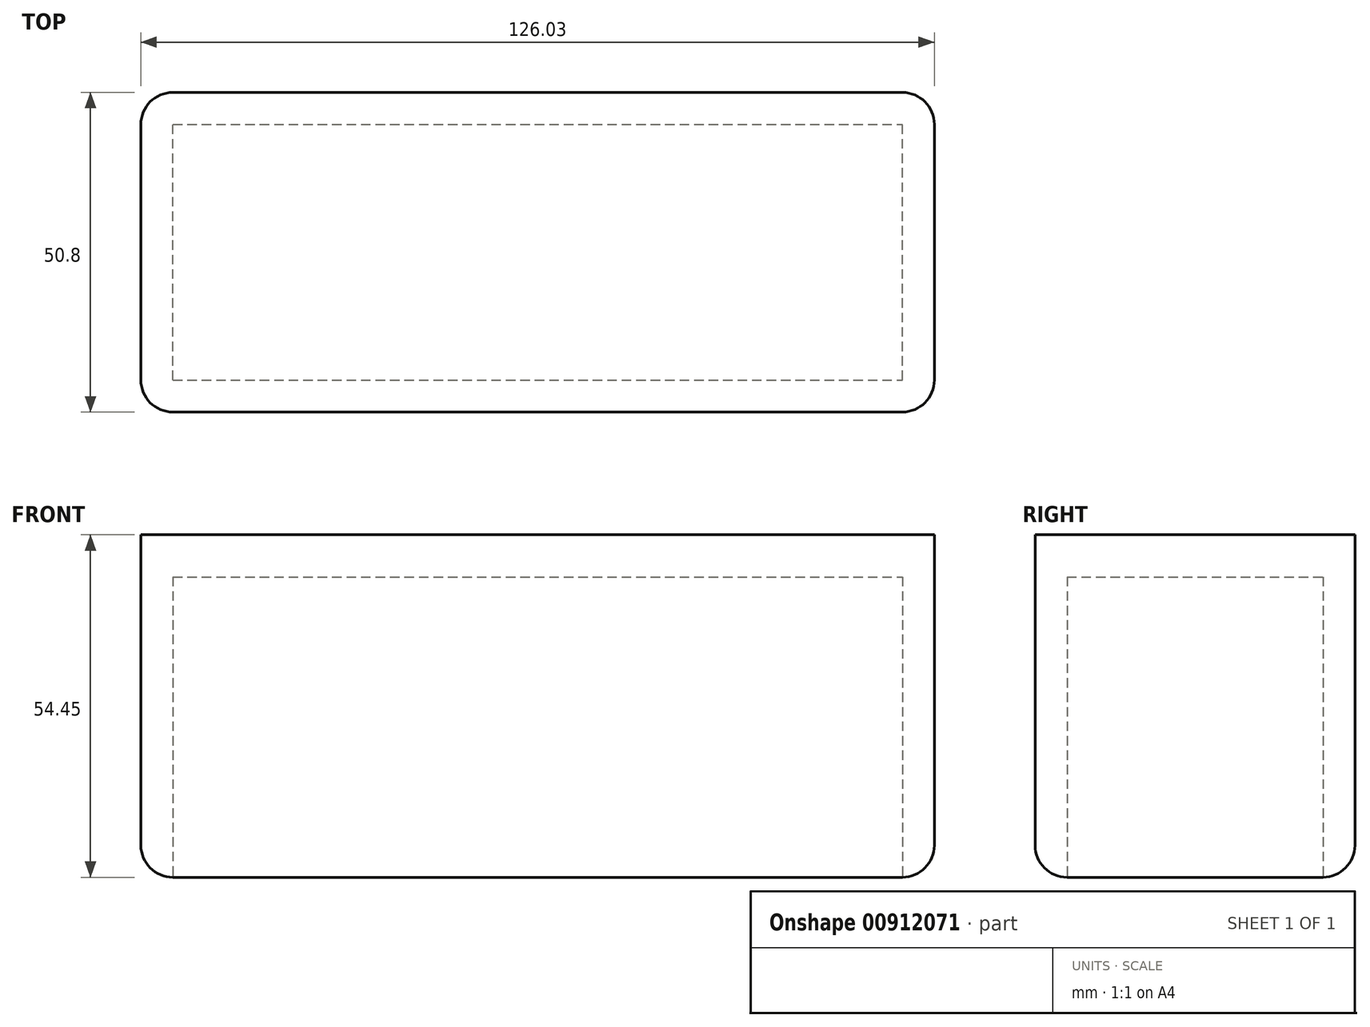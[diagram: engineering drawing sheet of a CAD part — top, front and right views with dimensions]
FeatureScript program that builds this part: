
annotation { "Feature Type Name" : "Feature", "Feature Type Description" : "" }
export const myFeature = defineFeature(function(context is Context, id is Id, definition is map)
    precondition{}
    {
        {
            var Q0;
            Q0=qCreatedBy(makeId("Front.planeOp"),FACE);
            var sketch = newSketch(context, id + "F0", { "sketchPlane" : qUnion([Q0])});
            skLineSegment(sketch, "E0.bottom", {"start": v(-59.7, 33.24) * mm, "end": v(66.32, 33.24) * mm});
            skLineSegment(sketch, "E0.top", {"start": v(-59.7, -21.2) * mm, "end": v(66.32, -21.2) * mm});
            skLineSegment(sketch, "E0.left", {"start": v(-59.7, 33.24) * mm, "end": v(-59.7, -21.2) * mm});
            skLineSegment(sketch, "E0.right", {"start": v(66.32, 33.24) * mm, "end": v(66.32, -21.2) * mm});
            skSolve(sketch);
        }
        {
            var Q0;
            Q0 = qSketchRegion(id + "F0", true);
            extrude(context, id + "F1", {"entities" : qUnion([Q0]), "depth" : 50.8 * mm, "offsetDistance" : 25.4 * mm});
        }
        {
            var Q0;
            Q0=makeQuery(id+"F1.opExtrude","CAP_EDGE",EDGE,{"disambiguationData":[OSD([sQuery(id+"F0.wireOp",EDGE,"E0.right")])],"isStart":false});
            var Q1;
            Q1=makeQuery(id+"F1.opExtrude","CAP_EDGE",EDGE,{"disambiguationData":[OSD([sQuery(id+"F0.wireOp",EDGE,"E0.left")])],"isStart":false});
            var Q2;
            Q2=makeQuery(id+"F1.opExtrude","CAP_EDGE",EDGE,{"disambiguationData":[OSD([sQuery(id+"F0.wireOp",EDGE,"E0.top")])],"isStart":false});
            var Q3;
            Q3=makeQuery(id+"F1.opExtrude","SWEPT_EDGE",EDGE,{"disambiguationData":[OSD([sQuery(id+"F0.wireOp",EDGE,"E0.top"),sQuery(id+"F0.wireOp",EDGE,"E0.left")])]});
            var Q4;
            Q4=makeQuery(id+"F1.opExtrude","SWEPT_EDGE",EDGE,{"disambiguationData":[OSD([sQuery(id+"F0.wireOp",EDGE,"E0.top"),sQuery(id+"F0.wireOp",EDGE,"E0.right")])]});
            var Q5;
            Q5=makeQuery(id+"F1.opExtrude","CAP_EDGE",EDGE,{"disambiguationData":[OSD([sQuery(id+"F0.wireOp",EDGE,"E0.top")])],"isStart":true});
            fillet(context, id + "F2", {"entities" : qUnion([Q0, Q1, Q2, Q3, Q4, Q5]), "radius" : 5.08 * mm, "tangentPropagation" : true, "allowEdgeOverflow" : false});
        }
        {
            var Q0;
            Q0=makeQuery(id+"F1.opExtrude","CAP_EDGE",EDGE,{"disambiguationData":[OSD([sQuery(id+"F0.wireOp",EDGE,"E0.right")])],"isStart":true});
            var Q1;
            Q1=makeQuery(id+"F1.opExtrude","CAP_EDGE",EDGE,{"disambiguationData":[OSD([sQuery(id+"F0.wireOp",EDGE,"E0.left")])],"isStart":true});
            fillet(context, id + "F3", {"entities" : qUnion([Q0, Q1]), "radius" : 5.08 * mm, "tangentPropagation" : true, "allowEdgeOverflow" : false});
        }
        {
            var Q0;
            Q0=makeQuery(id+"F1.opExtrude","SWEPT_FACE",FACE,{"disambiguationData":[OSD([sQuery(id+"F0.wireOp",EDGE,"E0.top")])]});
            extrude(context, id + "F4", {"entities" : qUnion([Q0]), "operationType" : NewBodyOperationType.REMOVE, "oppositeDirection" : true, "depth" : 47.75 * mm, "offsetDistance" : 25.4 * mm});
        }
    });
